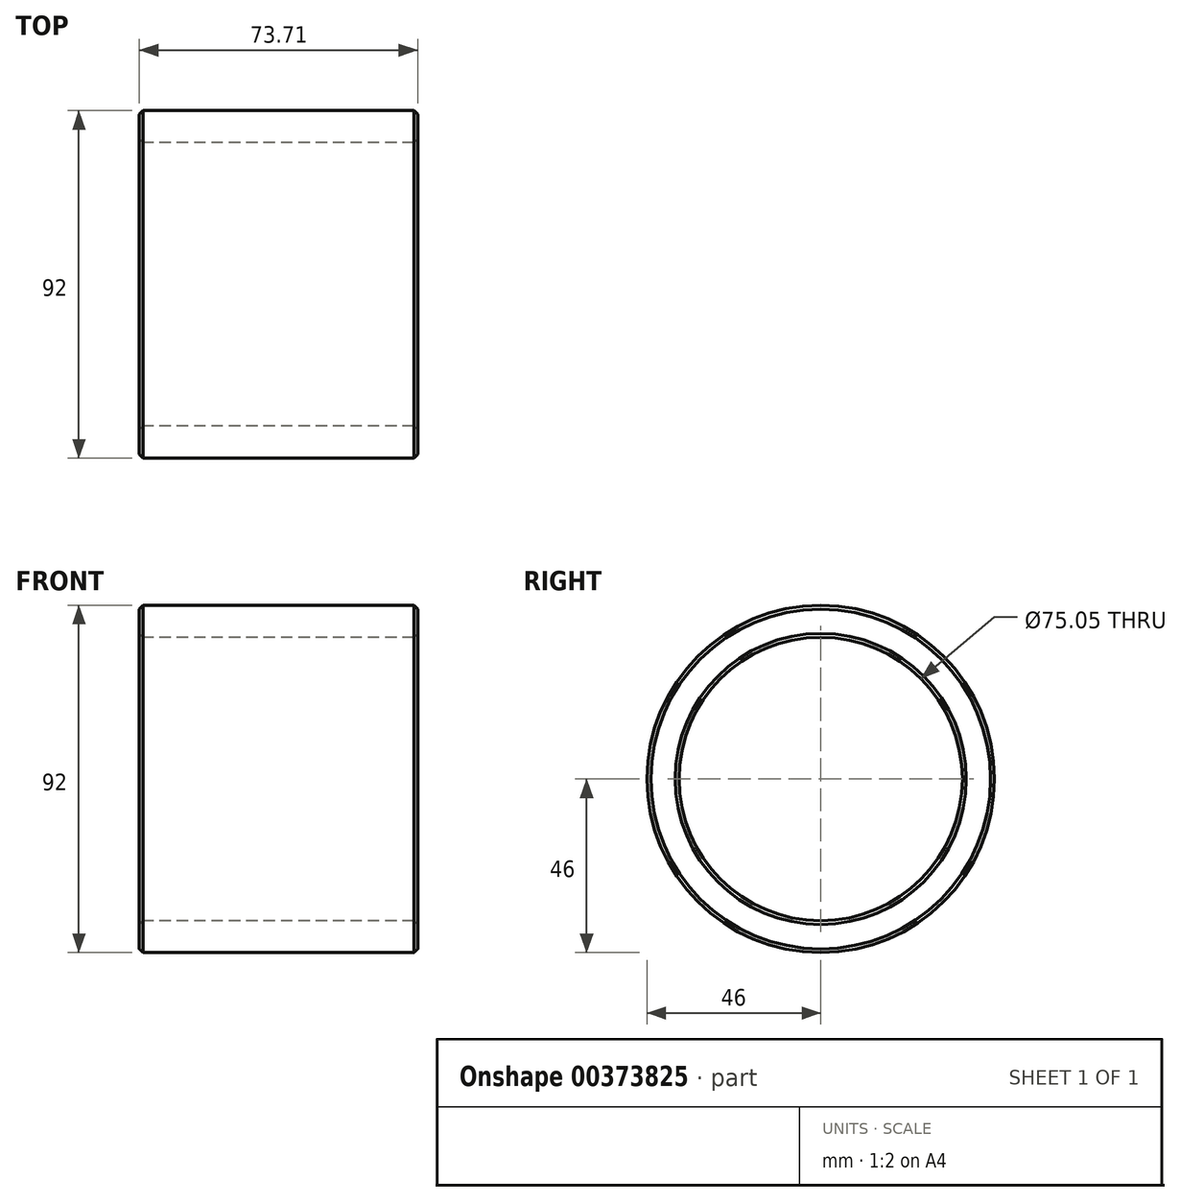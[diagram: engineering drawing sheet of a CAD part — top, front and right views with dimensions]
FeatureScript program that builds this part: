
annotation { "Feature Type Name" : "Feature", "Feature Type Description" : "" }
export const myFeature = defineFeature(function(context is Context, id is Id, definition is map)
    precondition{}
    {
        {
            var Q0;
            Q0=qCreatedBy(makeId("Right.planeOp"),FACE);
            var sketch = newSketch(context, id + "F0", { "sketchPlane" : qUnion([Q0])});
            skCircle(sketch, "E0", {"center": v(0, 0) * mm, "radius": 37.53 * mm});
            skCircle(sketch, "E1", {"center": v(0, 0) * mm, "radius": 46 * mm});
            skSolve(sketch);
        }
        {
            var Q0;
            Q0=qSketchRegion(id+"F0",true);
            extrude(context, id + "F1", {"entities" : qUnion([Q0]), "depth" : 73.7 * mm, "offsetDistance" : 25 * mm});
        }
        {
            var Q0;
            Q0=makeQuery(id+"F1.opExtrude","CAP_EDGE",EDGE,{"disambiguationData":[OSD([sQuery(id+"F0.wireOp",EDGE,"E1")])],"isStart":false});
            var Q1;
            Q1=makeQuery(id+"F1.opExtrude","CAP_EDGE",EDGE,{"disambiguationData":[OSD([sQuery(id+"F0.wireOp",EDGE,"E0")])],"isStart":false});
            var Q2;
            Q2=makeQuery(id+"F1.opExtrude","CAP_EDGE",EDGE,{"disambiguationData":[OSD([sQuery(id+"F0.wireOp",EDGE,"E1")])],"isStart":true});
            var Q3;
            Q3=makeQuery(id+"F1.opExtrude","CAP_EDGE",EDGE,{"disambiguationData":[OSD([sQuery(id+"F0.wireOp",EDGE,"E0")])],"isStart":true});
            chamfer(context, id + "F2", {"entities" : qUnion([Q0, Q1, Q2, Q3]), "width" : 1 * mm, "tangentPropagation" : true});
        }
    });
